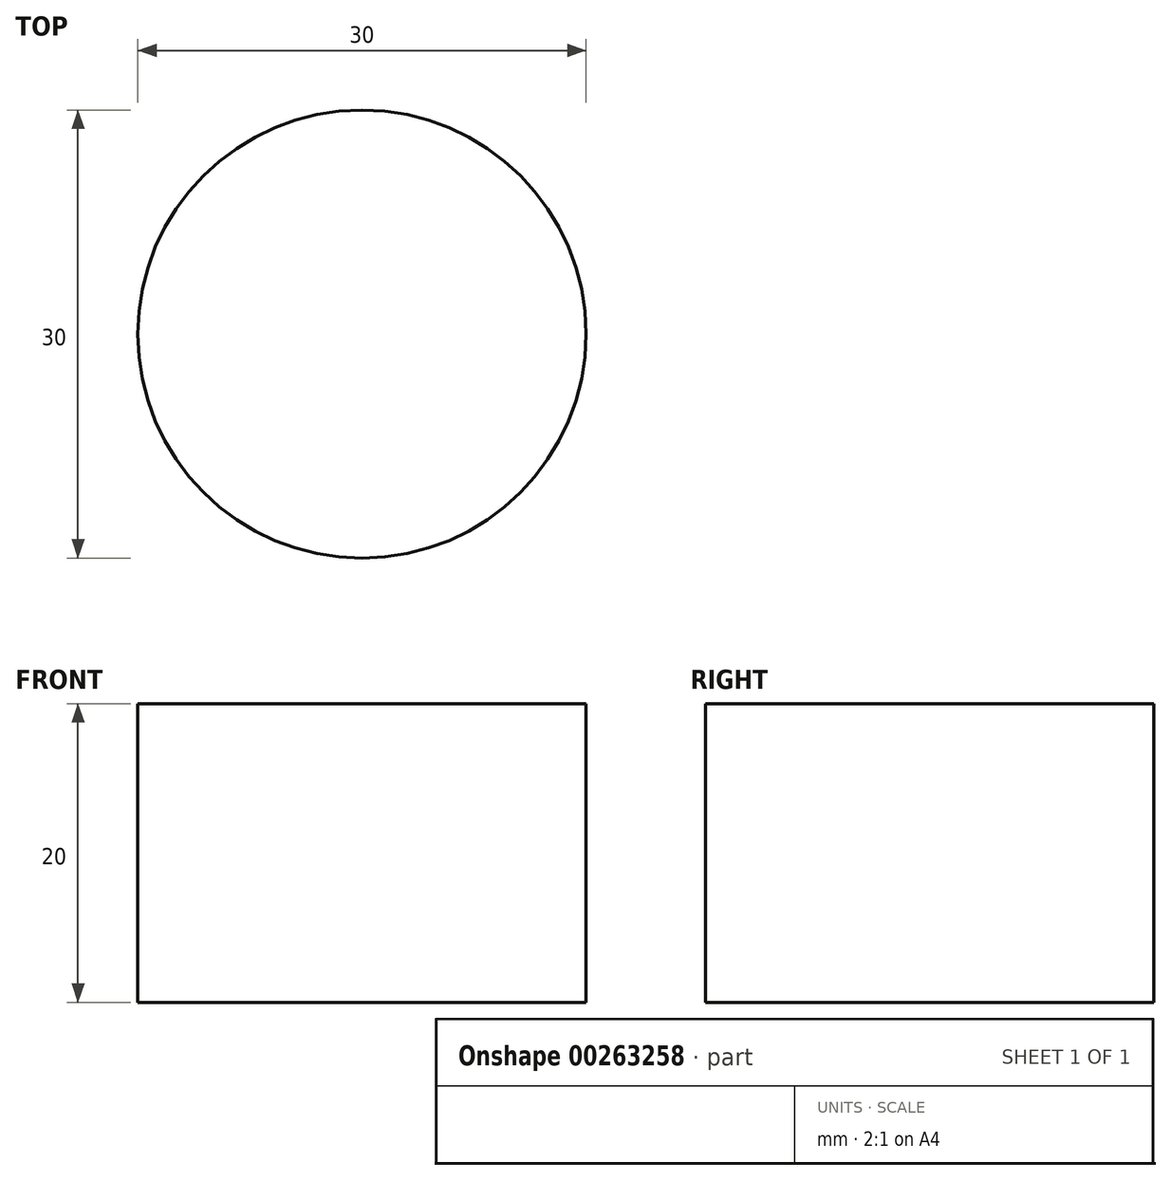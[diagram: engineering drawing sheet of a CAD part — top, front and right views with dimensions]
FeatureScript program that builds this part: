
annotation { "Feature Type Name" : "Feature", "Feature Type Description" : "" }
export const myFeature = defineFeature(function(context is Context, id is Id, definition is map)
    precondition{}
    {
        {
            var Q0;
            Q0=qCreatedBy(makeId("Top.planeOp"),FACE);
            var sketch = newSketch(context, id + "F0", { "sketchPlane" : qUnion([Q0])});
            skCircle(sketch, "E0", {"center": v(0, 1.49) * mm, "radius": 15 * mm});
            skSolve(sketch);
        }
        {
            var Q0;
            Q0 = qSketchRegion(id + "F0", true);
            extrude(context, id + "F1", {"entities" : qUnion([Q0]), "depth" : 20 * mm});
        }
    });
